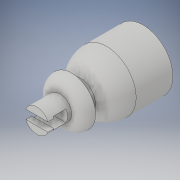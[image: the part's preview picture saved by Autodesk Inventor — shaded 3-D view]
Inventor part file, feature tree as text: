
AUTODESK INVENTOR PART (.ipt)
format: ipt  version: 2018 (Build 220112000, 112)  size: 196,096 bytes
history: native  units: mm
features: extrude x10, sketch x10, fillet x2
ambient origin geometry x8: Origin, YZ Plane, XZ Plane, XY Plane, X Axis, Y Axis, Z Axis, Center Point
bodies: Volumenkörper1 (feature_tree), Volumenkörper2 (feature_tree)
feature tree (22):
  extrude  "Extrusion1"  Depth=2.0mm TaperAngle=0.0deg
  fillet  "Rundung1"  Radius=2.0mm
  extrude  "Extrusion2"  Depth=5.0mm TaperAngle=0.0deg
  extrude  "Extrusion3"  Depth=10.0mm TaperAngle=0.0deg
  extrude  "Extrusion5"  Depth=2.5mm TaperAngle=0.0deg
  extrude  "Extrusion6"  Depth=2.5mm TaperAngle=0.0deg
  extrude  "Extrusion7"  Depth=1.6mm TaperAngle=0.0deg
  fillet  "Rundung2"  Radius=5.0mm
  extrude  "Extrusion10"  Depth=4.85mm TaperAngle=0.0deg
  extrude  "Extrusion11"  Depth=2.15mm TaperAngle=0.0deg
  extrude  "Extrusion12"  Depth=1.0mm TaperAngle=0.0deg
  extrude  "Extrusion13"  Depth=1.0mm
  sketch  "Skizze1"  dims[d0=8.0mm d1=2.0mm d2=0.0mm d3=2.0mm]
  sketch  "Skizze2"  dims[d4=5.0mm d5=1.5mm d6=0.0mm]
  sketch  "Skizze3"  dims[d7=10.0mm d8=8.0mm d9=0.0mm]
  sketch  "Skizze5"  dims[d13=10.0mm d14=2.5mm d15=0.0mm]
  sketch  "Skizze6"  dims[d16=8.5mm d17=2.5mm d18=0.0mm]
  sketch  "Skizze8"  dims[d19=1.6mm d20=1.6mm d21=0.0mm d22=5.0mm]
  sketch  "Skizze11"  dims[d23=4.0mm d28=4.85mm d29=0.0mm]
  sketch  "Skizze15"  dims[d30=2.0mm d31=2.15mm d32=0.0mm]
  sketch  "Skizze16"  dims[d33=4.0mm d34=1.0mm d35=0.0mm]
  sketch  "Skizze17"  dims[d36=1.0mm d37=0.0mm d26=1.0mm d27=1.0mm]
